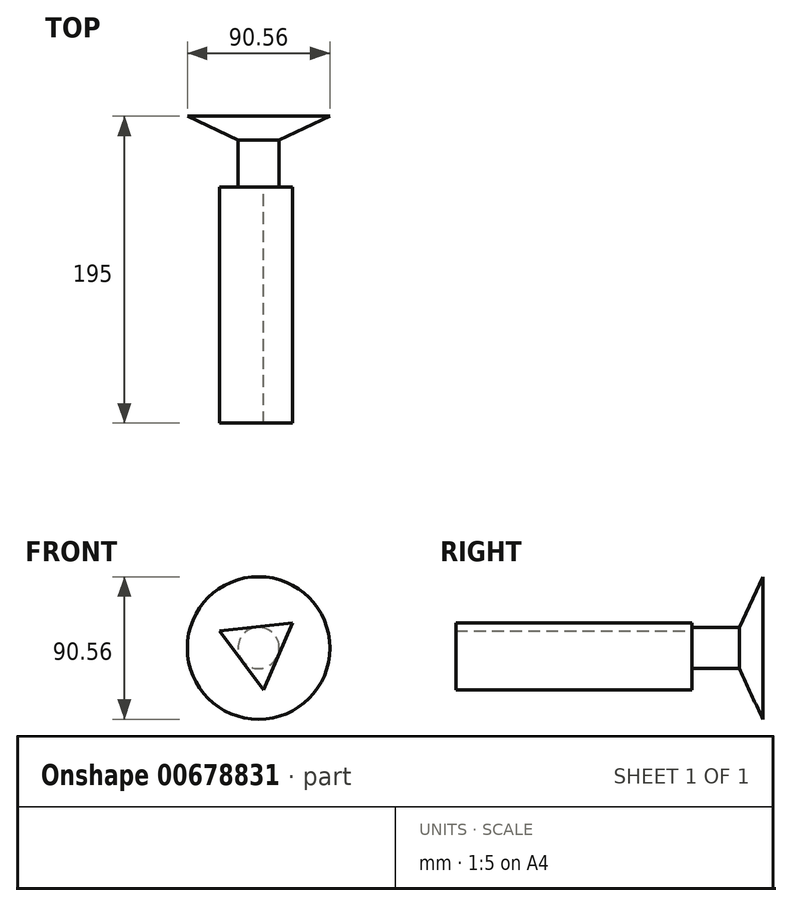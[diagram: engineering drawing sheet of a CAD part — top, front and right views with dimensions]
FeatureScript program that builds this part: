
annotation { "Feature Type Name" : "Feature", "Feature Type Description" : "" }
export const myFeature = defineFeature(function(context is Context, id is Id, definition is map)
    precondition{}
    {
        {
            var Q0;
            Q0=qCreatedBy(makeId("Front.planeOp"),FACE);
            var sketch = newSketch(context, id + "F0", { "sketchPlane" : qUnion([Q0])});
            skLineSegment(sketch, "E0.0", {"start": v(3.04, -26.76) * mm, "end": v(-24.7, 10.75) * mm});
            skLineSegment(sketch, "E0.1", {"start": v(-24.7, 10.75) * mm, "end": v(21.66, 16.02) * mm});
            skLineSegment(sketch, "E0.2", {"start": v(21.66, 16.02) * mm, "end": v(3.04, -26.76) * mm});
            skSolve(sketch);
        }
        {
            var Q0;
            Q0=makeQuery(id+"F0.imprint","IMPRINT",FACE,{"disambiguationData":[TD([[makeQuery(id+"F0.imprint","IMPRINT",EDGE,{"derivedFrom":sQuery(id+"F0.wireOp",EDGE,"E0.0")}),-1.0]])]});
            extrude(context, id + "F1", {"entities" : qUnion([Q0]), "depth" : 150 * mm, "offsetDistance" : 25 * mm});
        }
        {
            var Q0;
            Q0=qCreatedBy(makeId("Front.planeOp"),FACE);
            var sketch = newSketch(context, id + "F2", { "sketchPlane" : qUnion([Q0])});
            skCircle(sketch, "E1", {"center": v(0, 0) * mm, "radius": 13.12 * mm});
            skSolve(sketch);
        }
        {
            var Q0;
            Q0=makeQuery(id+"F2.imprint","IMPRINT",FACE,{"disambiguationData":[TD([[makeQuery(id+"F2.imprint","IMPRINT",EDGE,{"derivedFrom":sQuery(id+"F2.wireOp",EDGE,"E1")}),1.0]])]});
            extrude(context, id + "F3", {"entities" : qUnion([Q0]), "operationType" : NewBodyOperationType.ADD, "oppositeDirection" : true, "depth" : 30 * mm, "offsetDistance" : 25 * mm});
        }
        {
            var Q0;
            Q0=makeQuery(id+"F3.opExtrude","CAP_FACE",FACE,{"disambiguationData":[OSD([sQuery(id+"F2.wireOp",EDGE,"E1")])],"isStart":false});
            extrude(context, id + "F4", {"entities" : qUnion([Q0]), "operationType" : NewBodyOperationType.ADD, "depth" : 15 * mm, "offsetDistance" : 25 * mm, "hasDraft" : true, "draftAngle" : 65 * degree});
        }
    });
